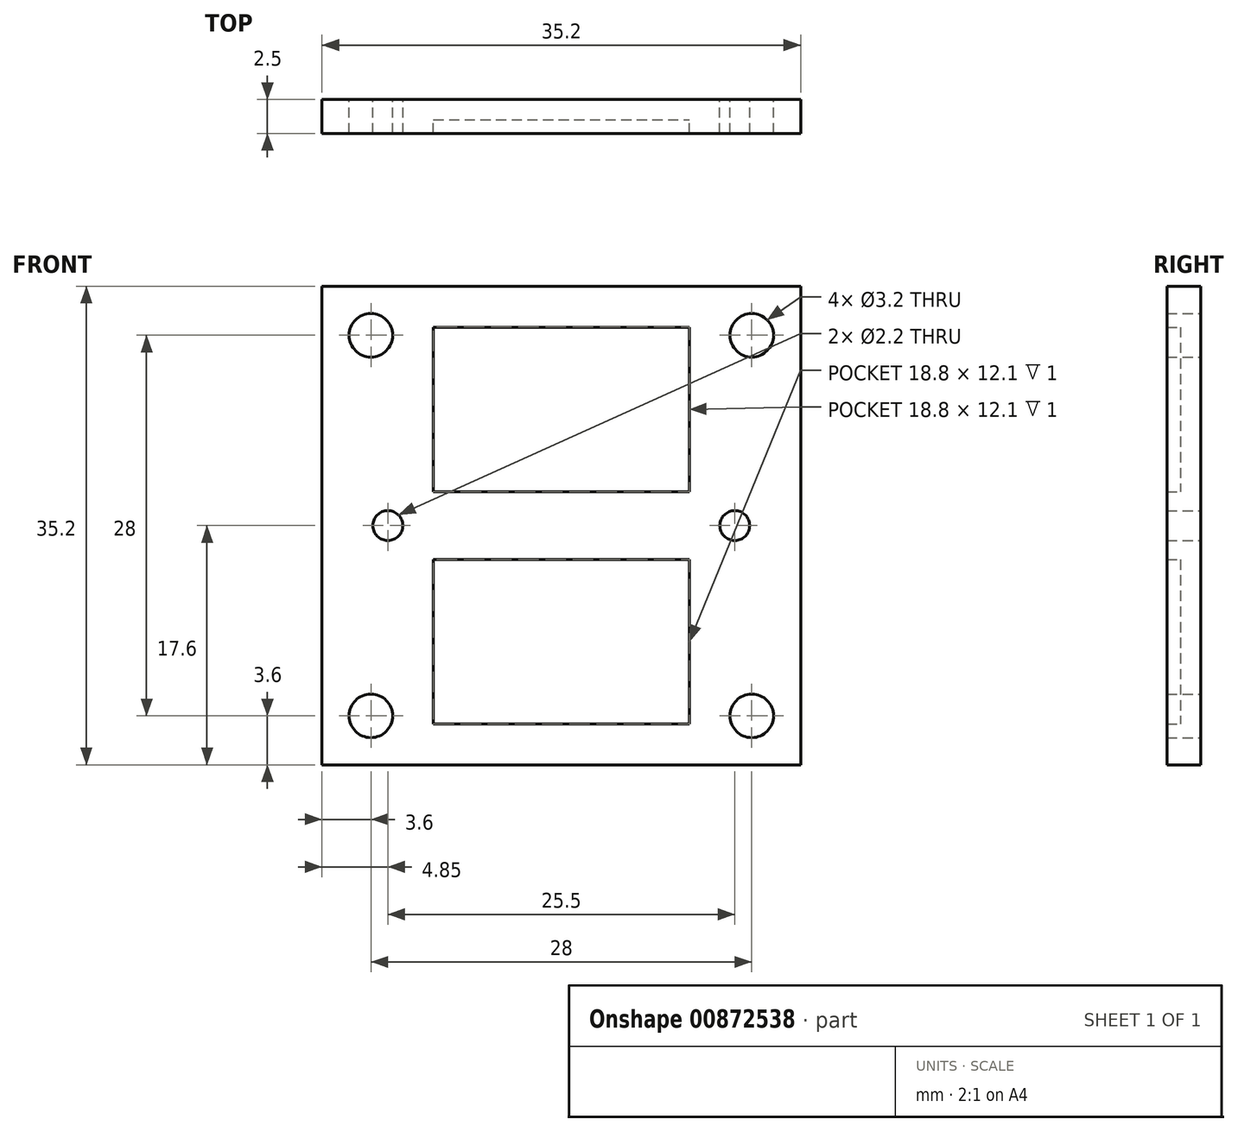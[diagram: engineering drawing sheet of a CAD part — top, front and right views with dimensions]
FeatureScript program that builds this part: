
annotation { "Feature Type Name" : "Feature", "Feature Type Description" : "" }
export const myFeature = defineFeature(function(context is Context, id is Id, definition is map)
    precondition{}
    {
        {
            var Q0;
            Q0=qCreatedBy(makeId("Front.planeOp"),FACE);
            var sketch = newSketch(context, id + "F0", { "sketchPlane" : qUnion([Q0])});
            skLineSegment(sketch, "E0.bottom", {"start": v(-17.6, 17.6) * mm, "end": v(17.6, 17.6) * mm});
            skLineSegment(sketch, "E0.top", {"start": v(-17.6, -17.6) * mm, "end": v(17.6, -17.6) * mm});
            skLineSegment(sketch, "E0.left", {"start": v(-17.6, 17.6) * mm, "end": v(-17.6, -17.6) * mm});
            skLineSegment(sketch, "E0.right", {"start": v(17.6, 17.6) * mm, "end": v(17.6, -17.6) * mm});
            skCircle(sketch, "E1", {"center": v(-14, 14) * mm, "radius": 1.6 * mm});
            skCircle(sketch, "E2.MirrorC", {"center": v(14, 14) * mm, "radius": 1.6 * mm});
            skCircle(sketch, "E3.MirrorC", {"center": v(14, -14) * mm, "radius": 1.6 * mm});
            skCircle(sketch, "E4.MirrorC", {"center": v(-14, -14) * mm, "radius": 1.6 * mm});
            skCircle(sketch, "E5", {"center": v(-12.75, 0) * mm, "radius": 1.1 * mm});
            skCircle(sketch, "E6.MirrorC", {"center": v(12.75, 0) * mm, "radius": 1.1 * mm});
            skSolve(sketch);
        }
        {
            var Q0;
            Q0 = qSketchRegion(id + "F0", true);
            extrude(context, id + "F1", {"entities" : qUnion([Q0]), "depth" : 1.5 * mm, "offsetDistance" : 25 * mm});
        }
        {
            var Q0;
            Q0=makeQuery(id+"F1.opExtrude","CAP_FACE",FACE,{"disambiguationData":[OSD([sQuery(id+"F0.wireOp",EDGE,"E0.bottom"),sQuery(id+"F0.wireOp",EDGE,"E0.top"),sQuery(id+"F0.wireOp",EDGE,"E0.left"),sQuery(id+"F0.wireOp",EDGE,"E0.right"),sQuery(id+"F0.wireOp",EDGE,"E1"),sQuery(id+"F0.wireOp",EDGE,"E2.MirrorC"),sQuery(id+"F0.wireOp",EDGE,"E3.MirrorC"),sQuery(id+"F0.wireOp",EDGE,"E4.MirrorC"),sQuery(id+"F0.wireOp",EDGE,"E5"),sQuery(id+"F0.wireOp",EDGE,"E6.MirrorC")])],"isStart":false});
            var sketch = newSketch(context, id + "F2", { "sketchPlane" : qUnion([Q0])});
            skLineSegment(sketch, "E7.bottom", {"start": v(-9.4, 2.5) * mm, "end": v(9.4, 2.5) * mm});
            skLineSegment(sketch, "E7.top", {"start": v(-9.4, -2.5) * mm, "end": v(9.4, -2.5) * mm});
            skLineSegment(sketch, "E7.left", {"start": v(-17.6, 2.5) * mm, "end": v(-17.6, -2.5) * mm});
            skLineSegment(sketch, "E7.right", {"start": v(17.6, 2.5) * mm, "end": v(17.6, -2.5) * mm});
            skLineSegment(sketch, "E8.bottom", {"start": v(-17.6, 17.6) * mm, "end": v(-9.4, 17.6) * mm});
            skLineSegment(sketch, "E8.top", {"start": v(-17.6, -17.6) * mm, "end": v(-9.4, -17.6) * mm});
            skLineSegment(sketch, "E8.left", {"start": v(-17.6, 17.6) * mm, "end": v(-17.6, -17.6) * mm});
            skLineSegment(sketch, "E8.right", {"start": v(-9.4, 14.6) * mm, "end": v(-9.4, 2.5) * mm});
            skLineSegment(sketch, "E9.bottom", {"start": v(17.6, 17.6) * mm, "end": v(9.4, 17.6) * mm});
            skLineSegment(sketch, "E9.top", {"start": v(17.6, -17.6) * mm, "end": v(9.4, -17.6) * mm});
            skLineSegment(sketch, "E9.left", {"start": v(17.6, 17.6) * mm, "end": v(17.6, -17.6) * mm});
            skLineSegment(sketch, "E9.right", {"start": v(9.4, 14.6) * mm, "end": v(9.4, 2.5) * mm});
            skLineSegment(sketch, "E10", {"start": v(-9.4, 17.6) * mm, "end": v(9.4, 17.6) * mm});
            skLineSegment(sketch, "E11", {"start": v(9.4, 14.6) * mm, "end": v(-9.4, 14.6) * mm});
            skLineSegment(sketch, "E12.MirrorCS", {"start": v(9.4, -14.6) * mm, "end": v(-9.4, -14.6) * mm});
            skLineSegment(sketch, "E13.MirrorCS", {"start": v(-9.4, -17.6) * mm, "end": v(9.4, -17.6) * mm});
            skLineSegment(sketch, "E14.trimOffspring", {"start": v(-9.4, -2.5) * mm, "end": v(-9.4, -14.6) * mm});
            skLineSegment(sketch, "E15.trimOffspring", {"start": v(9.4, -2.5) * mm, "end": v(9.4, -14.6) * mm});
            skCircle(sketch, "E16", {"center": v(-14, 14) * mm, "radius": 1.6 * mm});
            skCircle(sketch, "E17", {"center": v(-12.75, 0) * mm, "radius": 1.1 * mm});
            skCircle(sketch, "E18", {"center": v(-14, -14) * mm, "radius": 1.6 * mm});
            skCircle(sketch, "E19.MirrorC", {"center": v(14, -14) * mm, "radius": 1.6 * mm});
            skCircle(sketch, "E20.MirrorC", {"center": v(12.75, 0) * mm, "radius": 1.1 * mm});
            skCircle(sketch, "E21.MirrorC", {"center": v(14, 14) * mm, "radius": 1.6 * mm});
            skSolve(sketch);
        }
        {
            var Q0;
            Q0 = qSketchRegion(id + "F2", true);
            extrude(context, id + "F3", {"entities" : qUnion([Q0]), "operationType" : NewBodyOperationType.ADD, "depth" : 1 * mm, "offsetDistance" : 25 * mm});
        }
    });
